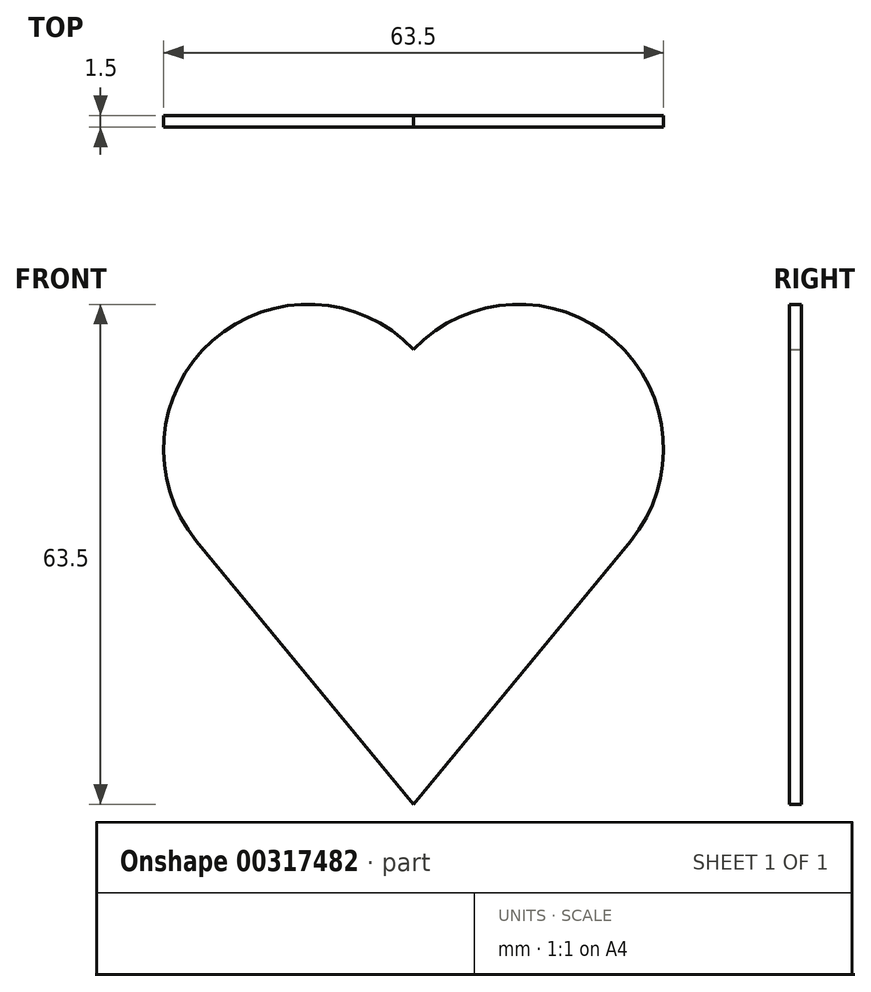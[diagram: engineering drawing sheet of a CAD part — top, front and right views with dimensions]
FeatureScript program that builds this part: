
annotation { "Feature Type Name" : "Feature", "Feature Type Description" : "" }
export const myFeature = defineFeature(function(context is Context, id is Id, definition is map)
    precondition{}
    {
        {
            var Q0;
            Q0=qCreatedBy(makeId("Front.planeOp"),FACE);
            var sketch = newSketch(context, id + "F0", { "sketchPlane" : qUnion([Q0])});
            skArc(sketch, "E0", {"start": v(27.54, 1.64) * mm, "mid": v(25.54, 27.13) * mm, "end": v(0, 26.01) * mm});
            skLineSegment(sketch, "E1", {"start": v(0, 26.01) * mm, "end": v(0, -31.75) * mm});
            skLineSegment(sketch, "E2", {"start": v(0, -31.75) * mm, "end": v(27.54, 1.64) * mm});
            skArc(sketch, "E3.MirrorCS", {"start": v(-27.54, 1.64) * mm, "mid": v(-25.54, 27.13) * mm, "end": v(0, 26.01) * mm});
            skLineSegment(sketch, "E4.MirrorCS", {"start": v(0, -31.75) * mm, "end": v(-27.54, 1.64) * mm});
            skPoint(sketch, "E5", {"position": v(13.35, 31.75) * mm});
            skPoint(sketch, "E6", {"position": v(31.75, 13.35) * mm});
            skLineSegment(sketch, "E7", {"start": v(0, -31.75) * mm, "end": v(0, -69.85) * mm, "construction": true});
            skLineSegment(sketch, "E8", {"start": v(0, -31.75) * mm, "end": v(6.35, -31.75) * mm, "construction": true});
            skLineSegment(sketch, "E9", {"start": v(6.35, -31.75) * mm, "end": v(6.35, -24.05) * mm, "construction": true});
            skLineSegment(sketch, "E10", {"start": v(6.35, -24.05) * mm, "end": v(0, -69.85) * mm});
            skLineSegment(sketch, "E11.MirrorCS", {"start": v(-6.35, -24.05) * mm, "end": v(0, -69.85) * mm});
            skLineSegment(sketch, "E12", {"start": v(0, -31.75) * mm, "end": v(0, -33.75) * mm});
            skLineSegment(sketch, "E13", {"start": v(0, -33.75) * mm, "end": v(6.02, -26.46) * mm});
            skLineSegment(sketch, "E14.MirrorCS", {"start": v(0, -33.75) * mm, "end": v(-6.02, -26.46) * mm});
            skSolve(sketch);
        }
        {
            var Q0;
            {var subQ0=sQuery(id+"F0.wireOp",EDGE,"E1");Q0=makeQuery(id+"F0.imprint","IMPRINT",FACE,{"disambiguationData":[TD([[makeQuery(id+"F0.imprint","IMPRINT",EDGE,{"derivedFrom":subQ0}),-1.0]])]});}
            var Q1;
            {var subQ0=sQuery(id+"F0.wireOp",EDGE,"E0");Q1=makeQuery(id+"F0.imprint","IMPRINT",FACE,{"disambiguationData":[TD([[makeQuery(id+"F0.imprint","IMPRINT",EDGE,{"derivedFrom":subQ0}),1.0]])]});}
            extrude(context, id + "F1", {"entities" : qUnion([Q0, Q1]), "depth" : 1.5 * mm});
        }
    });
